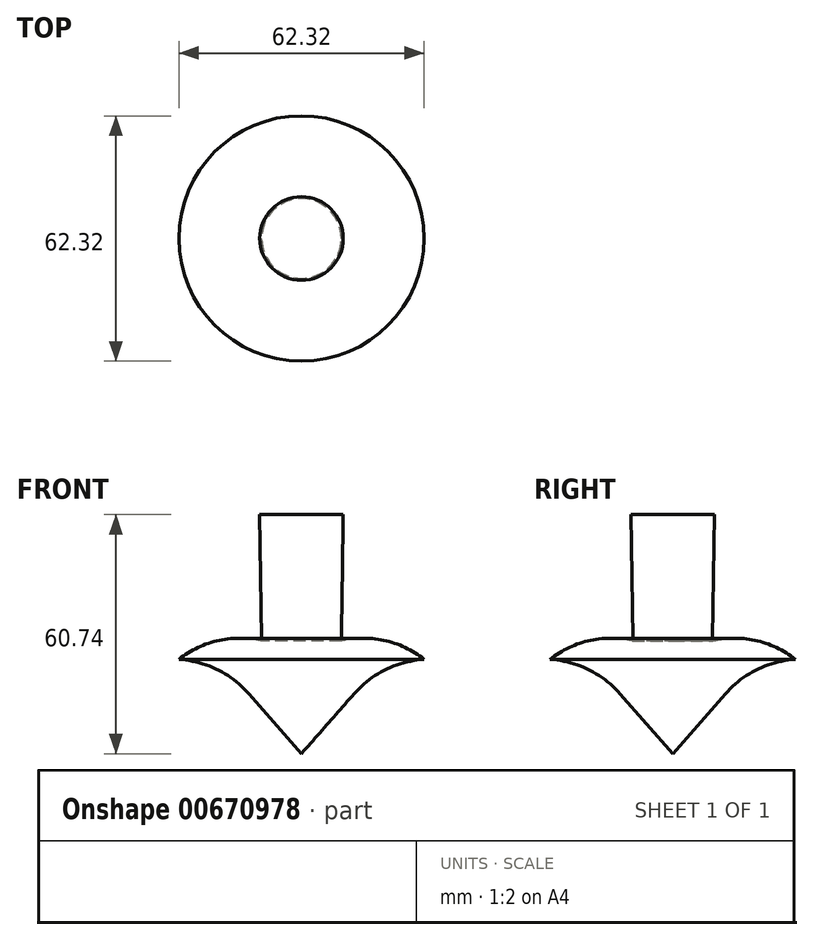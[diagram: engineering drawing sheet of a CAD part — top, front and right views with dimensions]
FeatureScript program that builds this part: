
annotation { "Feature Type Name" : "Feature", "Feature Type Description" : "" }
export const myFeature = defineFeature(function(context is Context, id is Id, definition is map)
    precondition{}
    {
        {
            var Q0;
            Q0=qCreatedBy(makeId("Front.planeOp"),FACE);
            var sketch = newSketch(context, id + "F0", { "sketchPlane" : qUnion([Q0])});
            skLineSegment(sketch, "E0", {"start": v(0, 0) * mm, "end": v(13.37, 15.2) * mm});
            skArc(sketch, "E1", {"start": v(13.37, 15.2) * mm, "mid": v(21.4, 21.35) * mm, "end": v(31.16, 23.96) * mm});
            skArc(sketch, "E2", {"start": v(31.16, 23.96) * mm, "mid": v(21.24, 28.73) * mm, "end": v(10.23, 28.67) * mm});
            skLineSegment(sketch, "E3", {"start": v(10.23, 28.67) * mm, "end": v(10.13, 28.67) * mm});
            skLineSegment(sketch, "E4", {"start": v(10.6, 60.74) * mm, "end": v(0, 60.74) * mm});
            skLineSegment(sketch, "E5", {"start": v(0, 60.74) * mm, "end": v(0, 0) * mm});
            skLineSegment(sketch, "E6", {"start": v(10.6, 60.74) * mm, "end": v(10.13, 28.67) * mm});
            skSolve(sketch);
        }
        {
            var Q0;
            Q0=qSketchRegion(id+"F0",true);
            var Q1;
            Q1=sQuery(id+"F0.wireOp",EDGE,"E5");
            revolve(context, id + "F1", {"entities" : qUnion([Q0]), "axis" : qUnion([Q1]), "revolveType" : RevolveType.FULL});
        }
    });
